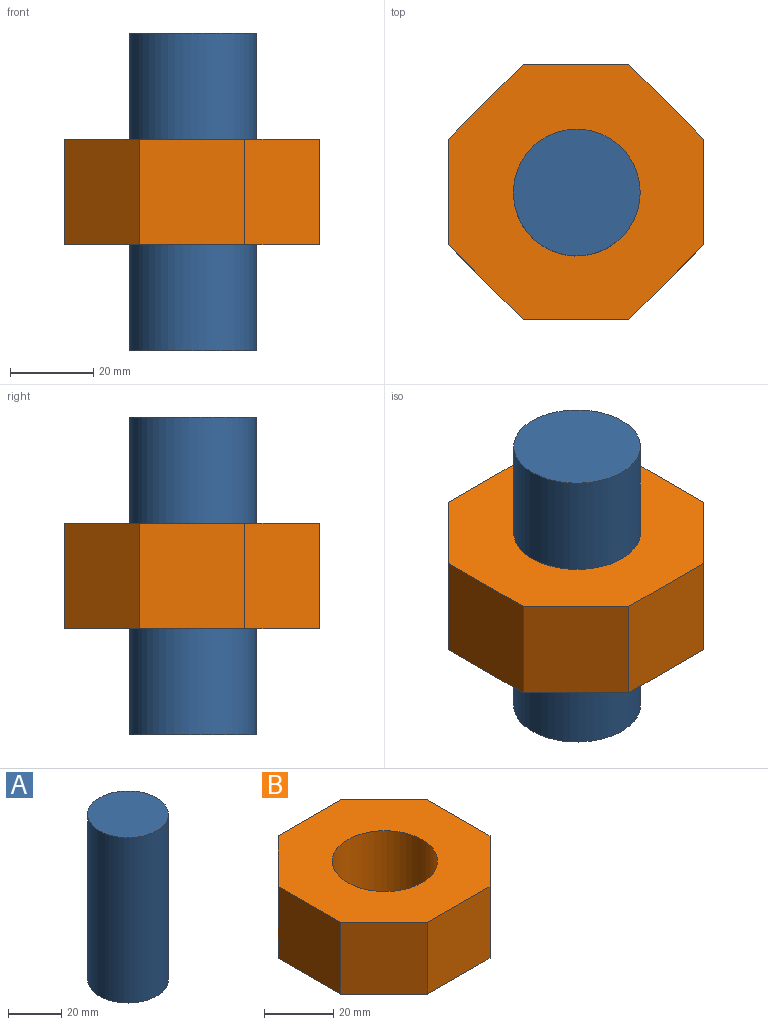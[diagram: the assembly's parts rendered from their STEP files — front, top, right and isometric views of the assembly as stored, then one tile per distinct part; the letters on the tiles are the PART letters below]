
ASSEMBLY  parts=2 mates=1
PART A: 3 faces, bbox 30.5x30.5x76.2 mm
  f0: cylinder r=15.24mm len=76.2mm, axis (0,0,-1), area 7296.6mm2, adj f1,f2
  f1: plane 30.48x30.48mm, normal (0,0,1), area 729.7mm2, adj f0
  f2: plane 30.48x30.48mm, normal (0,0,-1), area 729.7mm2, adj f0
PART B: 11 faces, bbox 61.3x61.3x25.4 mm
  f0: plane 25.4x17.96mm, normal (-0.71,0.71,0), area 645.2mm2, adj f1,f8,f9,f10
  f1: plane 25.4x25.4mm, normal (-1,0,0), area 645.2mm2, adj f0,f2,f9,f10
  f2: plane 25.4x17.96mm, normal (-0.71,-0.71,0), area 645.2mm2, adj f1,f3,f9,f10
  f3: plane 25.4x25.4mm, normal (0,-1,0), area 645.2mm2, adj f2,f4,f9,f10
  f4: plane 25.4x17.96mm, normal (0.71,-0.71,0), area 645.2mm2, adj f3,f5,f9,f10
  f5: plane 25.4x25.4mm, normal (1,0,0), area 645.2mm2, adj f4,f6,f9,f10
  f6: plane 25.4x17.96mm, normal (0.71,0.71,0), area 645.2mm2, adj f5,f8,f9,f10
  f7: cylinder r=15.24mm len=30.48mm, axis (0,0,-1), area 2432.2mm2, adj f9,f10
  f8: plane 25.4x25.4mm, normal (0,1,0), area 645.2mm2, adj f0,f6,f9,f10
  f9: plane 61.32x61.32mm, normal (0,0,1), area 2385.4mm2, adj f0,f1,f2,f3,f4,f5,f6,f7
  f10: plane 61.32x61.32mm, normal (0,0,-1), area 2385.4mm2, adj f0,f1,f2,f3,f4,f5,f6,f7
PLACE A t=(-142.82,-64.97,-11.87)mm
PLACE B t=(-142.82,-64.97,13.53)mm
MATE fastened B.f7 <-> A.f0  axis (0,0,-1) through (-142.82,-64.97,26.23)mm
